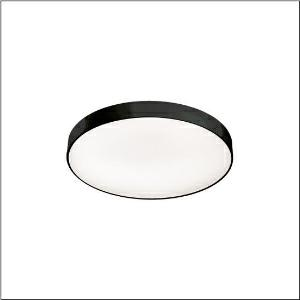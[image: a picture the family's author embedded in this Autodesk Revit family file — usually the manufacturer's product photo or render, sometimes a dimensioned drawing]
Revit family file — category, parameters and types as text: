
# Revit family: round_21_m_51mr36nd0421b
name_source: partatom
category: Lighting Fixtures
units: mm (PartAtom-declared; Revit-internal decimal feet)

## family parameters
Cut with Voids When Loaded = No
Host = Face
Light Source = No
Part Type = Normal
Room Calculation Point = No
Round Connector Dimension = Use Diameter
Shared = No

## types (1)
- Round 21 M (1 x LED, 7470 lm, 54.6 W, 4000K)
    Apparent Load = 55 VA
    CIE Flux Codes = 66 90 98 84 100
    Color Rendering = 80
    Color Temperature = 4000K
    Default Elevation = 1800 mm
    Description = Round 21 M, wall and ceiling luminaire, primary optical cover: micro prismatic cover, of PMMA, transparent, CAT 2 (L<= 3000cd/m²), light emission: direct/indirect distribution, primary light characteristic: symmetric, installation type: surface-mounted, suspended mounting, LED, rated luminous flux: 7.470lm, luminous efficacy: 137lm/W, light colour: 840, colour temperature: 4000K, control gear: DALI 2, with terminal, 5-pole, mains connection: 230V, AC, 50/60Hz, rated input power: 54.6W, housing, of aluminium, coated, black, diameter: 600mm, height: 62mm, protection rating (complete): IP40, insulation class (complete): insulation class I (protective earthing), certification: CE, impact resistance: IK04, permissible operating ambient temperature: -10..+35°C, packaging unit: 1 piece
    Height = 87 mm
    Lamp = 1 x LED
    Lamp Light Flux = 7470 lm
    Lamp Power = 54.6 W
    Lamp count = 1
    Length = 600 mm
    Luminous efficacy = 137 lm/W
    Manufacturer = Siteco
    ModVariant = No
    Model = 51MR36ND0421B
    Mounting Place = Ceiling
    Mounting Type = Surface mounted
    Number of Poles = 1
    OnlyDefault = Yes
    Power Factor = 1
    Product Name = Round 21 M
    Product group = wall and ceiling luminaire | ceiling mounted
    ProductGroupID = 304
    Protection Class = Protection class I
    Protection Degree = IP 40
    RLX_Detail_Level = 1
    RLX_Emergency_Light_Flux = 0 lm
    RLX_Emergency_Type = 0
    RLX_Emergency_Type_DB = No
    RlxData = <blob elided: 22001 chars, md5=cee7a5a5>
    Socket = socket
    Standby Power = 0 W
    System Light Flux = 7470 lm
    System Power = 55 W
    Type Comments = Product without accessories
    Type Image = l_1258305.jpg
    URL = http://relux.com
    VarID = ---
    Voltage = 0 V
    Weight = 0.00 kg
    Width = 0 mm  [stored 0 ft]

note: [stored X ft] marks values corroborated as IEEE doubles in the binary element streams (Revit-internal decimal feet)

## geometry (parser evidence)
native form markers: Blend x4, Sweep x14
no freeform markers — native parametric forms only
